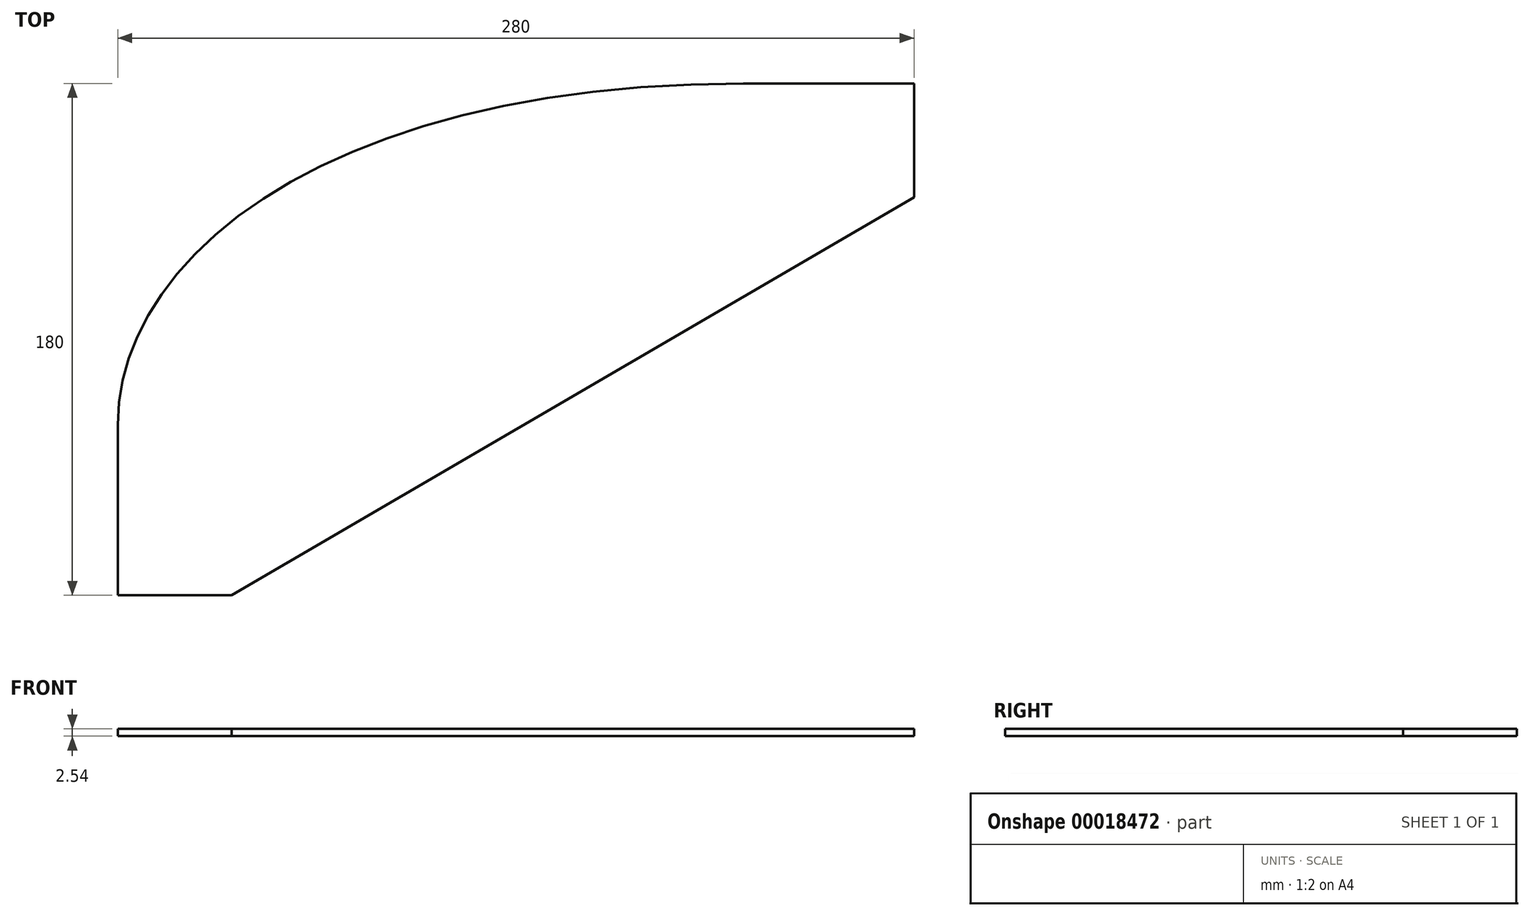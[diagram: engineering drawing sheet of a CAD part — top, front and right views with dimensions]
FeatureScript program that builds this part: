
annotation { "Feature Type Name" : "Feature", "Feature Type Description" : "" }
export const myFeature = defineFeature(function(context is Context, id is Id, definition is map)
    precondition{}
    {
        {
            var Q0;
            Q0=qCreatedBy(makeId("Top.planeOp"),FACE);
            var sketch = newSketch(context, id + "F0", { "sketchPlane" : qUnion([Q0])});
            skLineSegment(sketch, "E0.bottom", {"start": v(228.6, 228.6) * mm, "end": v(-228.6, 228.6) * mm});
            skLineSegment(sketch, "E0.top", {"start": v(228.6, -228.6) * mm, "end": v(-228.6, -228.6) * mm});
            skLineSegment(sketch, "E0.left", {"start": v(228.6, 228.6) * mm, "end": v(228.6, -228.6) * mm});
            skLineSegment(sketch, "E0.right", {"start": v(-228.6, 228.6) * mm, "end": v(-228.6, -228.6) * mm});
            skPoint(sketch, "E0.middle", {"position": v(0, 0) * mm});
            skSolve(sketch);
        }
        {
            var Q0;
            Q0=qSketchRegion(id+"F0",true);
            extrude(context, id + "F1", {"entities" : qUnion([Q0]), "depth" : 2.54 * mm});
        }
        {
            var Q0;
            Q0=makeQuery(id+"F1.opExtrude","SWEPT_EDGE",EDGE,{"disambiguationData":[OSD([sQuery(id+"F0.wireOp",EDGE,"E0.top"),sQuery(id+"F0.wireOp",EDGE,"E0.right")])]});
            var Q1;
            Q1=makeQuery(id+"F1.opExtrude","SWEPT_EDGE",EDGE,{"disambiguationData":[OSD([sQuery(id+"F0.wireOp",EDGE,"E0.top"),sQuery(id+"F0.wireOp",EDGE,"E0.left")])]});
            fillet(context, id + "F2", {"entities" : qUnion([Q0, Q1]), "radius" : 25.4 * mm, "tangentPropagation" : true, "allowEdgeOverflow" : false});
        }
        {
            var Q0;
            Q0=makeQuery(id+"F1.opExtrude","CAP_FACE",FACE,{"disambiguationData":[OSD([sQuery(id+"F0.wireOp",EDGE,"E0.bottom"),sQuery(id+"F0.wireOp",EDGE,"E0.top"),sQuery(id+"F0.wireOp",EDGE,"E0.left"),sQuery(id+"F0.wireOp",EDGE,"E0.right")])],"isStart":false});
            var sketch = newSketch(context, id + "F3", { "sketchPlane" : qUnion([Q0])});
            skLineSegment(sketch, "E1", {"start": v(-228.6, 108.6) * mm, "end": v(-228.6, 228.6) * mm});
            skLineSegment(sketch, "E2", {"start": v(-228.6, 228.6) * mm, "end": v(-8.6, 228.6) * mm});
            skFitSpline(sketch, "E3", {"points": [v(-228.6, 108.6) * mm, v(-8.6, 228.6) * mm], "startDerivative": vector(0, 180) * mm, "endDerivative": vector(433.06, 0) * mm});
            skSolve(sketch);
        }
        {
            var Q0;
            Q0 = qSketchRegion(id + "F3", true);
            extrude(context, id + "F4", {"entities" : qUnion([Q0]), "operationType" : NewBodyOperationType.REMOVE, "endBound" : BoundingType.UP_TO_NEXT, "oppositeDirection" : true, "depth" : 25 * mm});
        }
        {
            var Q0;
            Q0=makeQuery(id+"F1.opExtrude","CAP_FACE",FACE,{"disambiguationData":[OSD([sQuery(id+"F0.wireOp",EDGE,"E0.bottom"),sQuery(id+"F0.wireOp",EDGE,"E0.top"),sQuery(id+"F0.wireOp",EDGE,"E0.left"),sQuery(id+"F0.wireOp",EDGE,"E0.right")])],"isStart":false});
            var sketch = newSketch(context, id + "F5", { "sketchPlane" : qUnion([Q0])});
            skLineSegment(sketch, "E4", {"start": v(-228.6, 48.6) * mm, "end": v(-188.6, 48.6) * mm});
            skLineSegment(sketch, "E5", {"start": v(-188.6, 48.6) * mm, "end": v(51.4, 188.6) * mm});
            skLineSegment(sketch, "E6", {"start": v(51.4, 188.6) * mm, "end": v(51.4, 228.6) * mm});
            skLineSegment(sketch, "E7", {"start": v(51.4, 228.6) * mm, "end": v(228.6, 228.6) * mm});
            skLineSegment(sketch, "E8", {"start": v(228.6, 228.6) * mm, "end": v(228.6, -228.6) * mm});
            skLineSegment(sketch, "E9", {"start": v(228.6, -228.6) * mm, "end": v(-228.6, -228.6) * mm});
            skLineSegment(sketch, "E10", {"start": v(-228.6, -228.6) * mm, "end": v(-228.6, 48.6) * mm});
            skLineSegment(sketch, "E11", {"start": v(8.6, 228.6) * mm, "end": v(51.4, 228.6) * mm, "construction": true});
            skSolve(sketch);
        }
        {
            var Q0;
            Q0 = qSketchRegion(id + "F5", true);
            extrude(context, id + "F6", {"entities" : qUnion([Q0]), "operationType" : NewBodyOperationType.REMOVE, "endBound" : BoundingType.UP_TO_NEXT, "oppositeDirection" : true, "depth" : 25 * mm});
        }
    });
